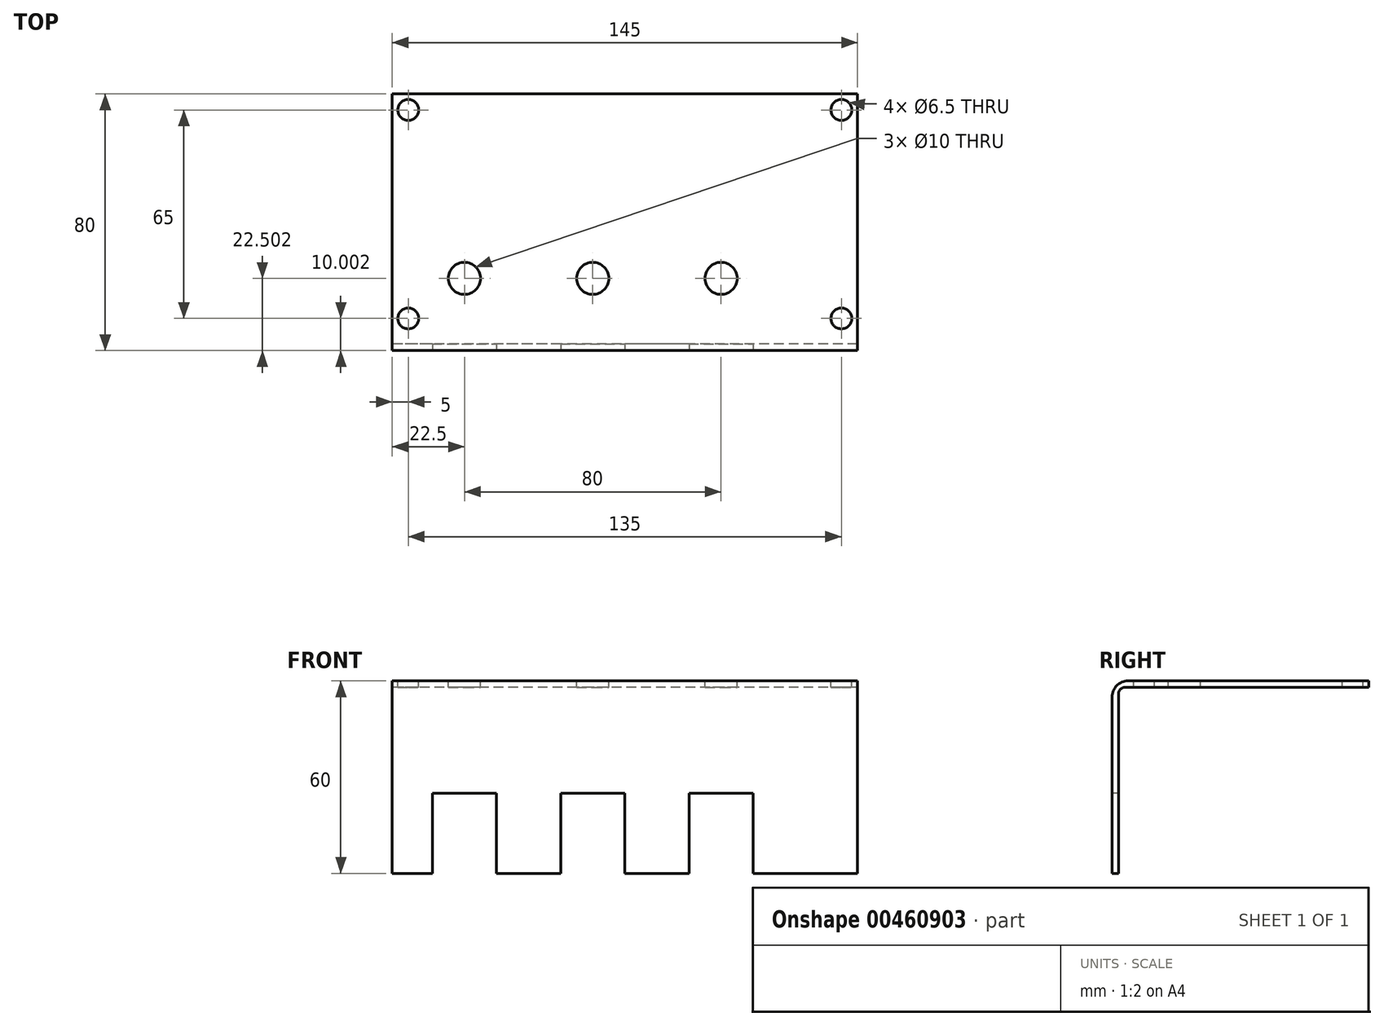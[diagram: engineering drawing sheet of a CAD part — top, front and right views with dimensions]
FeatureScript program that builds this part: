
annotation { "Feature Type Name" : "Feature", "Feature Type Description" : "" }
export const myFeature = defineFeature(function(context is Context, id is Id, definition is map)
    precondition{}
    {
        {
            var Q0;
            Q0=qCreatedBy(makeId("Right.planeOp"),FACE);
            var sketch = newSketch(context, id + "F0", { "sketchPlane" : qUnion([Q0])});
            skLineSegment(sketch, "E0", {"start": v(34.47, 55.47) * mm, "end": v(-40.53, 55.47) * mm});
            skLineSegment(sketch, "E1", {"start": v(-45.53, 50.47) * mm, "end": v(-45.53, -4.53) * mm});
            skLineSegment(sketch, "E2", {"start": v(-45.53, -4.53) * mm, "end": v(-43.53, -4.53) * mm});
            skLineSegment(sketch, "E3", {"start": v(-43.53, -4.53) * mm, "end": v(-43.53, 51.47) * mm});
            skLineSegment(sketch, "E4", {"start": v(-41.53, 53.47) * mm, "end": v(34.47, 53.47) * mm});
            skLineSegment(sketch, "E5", {"start": v(34.47, 53.47) * mm, "end": v(34.47, 55.47) * mm});
            skPoint(sketch, "E6.visualSharp", {"position": v(-43.53, 53.47) * mm});
            skArc(sketch, "E6.filletArc", {"start": v(-41.53, 53.47) * mm, "mid": v(-42.94, 52.88) * mm, "end": v(-43.53, 51.47) * mm});
            skPoint(sketch, "E7.visualSharp", {"position": v(-45.53, 55.47) * mm});
            skArc(sketch, "E7.filletArc", {"start": v(-40.53, 55.47) * mm, "mid": v(-44.06, 54) * mm, "end": v(-45.53, 50.47) * mm});
            skSolve(sketch);
        }
        {
            var Q0;
            Q0=makeQuery(id+"F0.imprint","IMPRINT",FACE,{"disambiguationData":[TD([[makeQuery(id+"F0.imprint","IMPRINT",EDGE,{"derivedFrom":sQuery(id+"F0.wireOp",EDGE,"E0")}),1.0]])]});
            extrude(context, id + "F1", {"entities" : qUnion([Q0]), "depth" : 145 * mm, "offsetDistance" : 25 * mm, "symmetric" : true});
        }
        {
            var Q0;
            Q0=makeQuery(id+"F1.opExtrude","SWEPT_FACE",FACE,{"disambiguationData":[OSD([sQuery(id+"F0.wireOp",EDGE,"E1")])]});
            var sketch = newSketch(context, id + "F2", { "sketchPlane" : qUnion([Q0])});
            skLineSegment(sketch, "E8.bottom", {"start": v(-20, 20.47) * mm, "end": v(0, 20.47) * mm});
            skLineSegment(sketch, "E8.top", {"start": v(-20, -4.53) * mm, "end": v(0, -4.53) * mm});
            skLineSegment(sketch, "E8.left", {"start": v(-20, 20.47) * mm, "end": v(-20, -4.53) * mm});
            skLineSegment(sketch, "E8.right", {"start": v(0, 20.47) * mm, "end": v(0, -4.53) * mm});
            skLineSegment(sketch, "E9.bottom", {"start": v(-60, 20.47) * mm, "end": v(-40, 20.47) * mm});
            skLineSegment(sketch, "E9.top", {"start": v(-60, -4.53) * mm, "end": v(-40, -4.53) * mm});
            skLineSegment(sketch, "E9.left", {"start": v(-60, 20.47) * mm, "end": v(-60, -4.53) * mm});
            skLineSegment(sketch, "E9.right", {"start": v(-40, 20.47) * mm, "end": v(-40, -4.53) * mm});
            skLineSegment(sketch, "E10.bottom", {"start": v(20, 20.47) * mm, "end": v(40, 20.47) * mm});
            skLineSegment(sketch, "E10.top", {"start": v(20, -4.53) * mm, "end": v(40, -4.53) * mm});
            skLineSegment(sketch, "E10.left", {"start": v(20, 20.47) * mm, "end": v(20, -4.53) * mm});
            skLineSegment(sketch, "E10.right", {"start": v(40, 20.47) * mm, "end": v(40, -4.53) * mm});
            skSolve(sketch);
        }
        {
            var Q0;
            Q0=makeQuery(id+"F2.imprint","IMPRINT",FACE,{"disambiguationData":[TD([[makeQuery(id+"F2.imprint","IMPRINT",EDGE,{"derivedFrom":sQuery(id+"F2.wireOp",EDGE,"E9.bottom")}),-1.0]])]});
            var Q1;
            Q1=makeQuery(id+"F2.imprint","IMPRINT",FACE,{"disambiguationData":[TD([[makeQuery(id+"F2.imprint","IMPRINT",EDGE,{"derivedFrom":sQuery(id+"F2.wireOp",EDGE,"E8.bottom")}),-1.0]])]});
            var Q2;
            Q2=makeQuery(id+"F2.imprint","IMPRINT",FACE,{"disambiguationData":[TD([[makeQuery(id+"F2.imprint","IMPRINT",EDGE,{"derivedFrom":sQuery(id+"F2.wireOp",EDGE,"E10.bottom")}),-1.0]])]});
            extrude(context, id + "F3", {"entities" : qUnion([Q0, Q1, Q2]), "operationType" : NewBodyOperationType.REMOVE, "oppositeDirection" : true, "depth" : 25 * mm, "offsetDistance" : 25 * mm});
        }
        {
            var Q0;
            Q0=makeQuery(id+"F1.opExtrude","SWEPT_FACE",FACE,{"disambiguationData":[OSD([sQuery(id+"F0.wireOp",EDGE,"E0")])]});
            var sketch = newSketch(context, id + "F4", { "sketchPlane" : qUnion([Q0])});
            skCircle(sketch, "E11", {"center": v(-50, -23.03) * mm, "radius": 5 * mm});
            skCircle(sketch, "E12", {"center": v(-10, -23.03) * mm, "radius": 5 * mm});
            skCircle(sketch, "E13", {"center": v(30, -23.03) * mm, "radius": 5 * mm});
            skSolve(sketch);
        }
        {
            var Q0;
            Q0=makeQuery(id+"F4.imprint","IMPRINT",FACE,{"disambiguationData":[TD([[makeQuery(id+"F4.imprint","IMPRINT",EDGE,{"derivedFrom":sQuery(id+"F4.wireOp",EDGE,"E11")}),1.0]])]});
            var Q1;
            Q1=makeQuery(id+"F4.imprint","IMPRINT",FACE,{"disambiguationData":[TD([[makeQuery(id+"F4.imprint","IMPRINT",EDGE,{"derivedFrom":sQuery(id+"F4.wireOp",EDGE,"E12")}),1.0]])]});
            var Q2;
            Q2=makeQuery(id+"F4.imprint","IMPRINT",FACE,{"disambiguationData":[TD([[makeQuery(id+"F4.imprint","IMPRINT",EDGE,{"derivedFrom":sQuery(id+"F4.wireOp",EDGE,"E13")}),1.0]])]});
            extrude(context, id + "F5", {"entities" : qUnion([Q0, Q1, Q2]), "operationType" : NewBodyOperationType.REMOVE, "oppositeDirection" : true, "depth" : 25 * mm, "offsetDistance" : 25 * mm});
        }
        {
            var Q0;
            Q0=makeQuery(id+"F1.opExtrude","SWEPT_FACE",FACE,{"disambiguationData":[OSD([sQuery(id+"F0.wireOp",EDGE,"E0")])]});
            var sketch = newSketch(context, id + "F6", { "sketchPlane" : qUnion([Q0])});
            skCircle(sketch, "E14", {"center": v(-67.5, 29.47) * mm, "radius": 3.25 * mm});
            skCircle(sketch, "E15", {"center": v(67.5, 29.47) * mm, "radius": 3.25 * mm});
            skCircle(sketch, "E16", {"center": v(67.5, -35.53) * mm, "radius": 3.25 * mm});
            skCircle(sketch, "E17", {"center": v(-67.5, -35.53) * mm, "radius": 3.25 * mm});
            skSolve(sketch);
        }
        {
            var Q0;
            Q0=makeQuery(id+"F6.imprint","IMPRINT",FACE,{"disambiguationData":[TD([[makeQuery(id+"F6.imprint","IMPRINT",EDGE,{"derivedFrom":sQuery(id+"F6.wireOp",EDGE,"E17")}),1.0]])]});
            var Q1;
            Q1=makeQuery(id+"F6.imprint","IMPRINT",FACE,{"disambiguationData":[TD([[makeQuery(id+"F6.imprint","IMPRINT",EDGE,{"derivedFrom":sQuery(id+"F6.wireOp",EDGE,"E14")}),1.0]])]});
            var Q2;
            Q2=makeQuery(id+"F6.imprint","IMPRINT",FACE,{"disambiguationData":[TD([[makeQuery(id+"F6.imprint","IMPRINT",EDGE,{"derivedFrom":sQuery(id+"F6.wireOp",EDGE,"E15")}),1.0]])]});
            var Q3;
            Q3=makeQuery(id+"F6.imprint","IMPRINT",FACE,{"disambiguationData":[TD([[makeQuery(id+"F6.imprint","IMPRINT",EDGE,{"derivedFrom":sQuery(id+"F6.wireOp",EDGE,"E16")}),1.0]])]});
            extrude(context, id + "F7", {"entities" : qUnion([Q0, Q1, Q2, Q3]), "operationType" : NewBodyOperationType.REMOVE, "oppositeDirection" : true, "depth" : 25 * mm, "offsetDistance" : 25 * mm});
        }
    });
